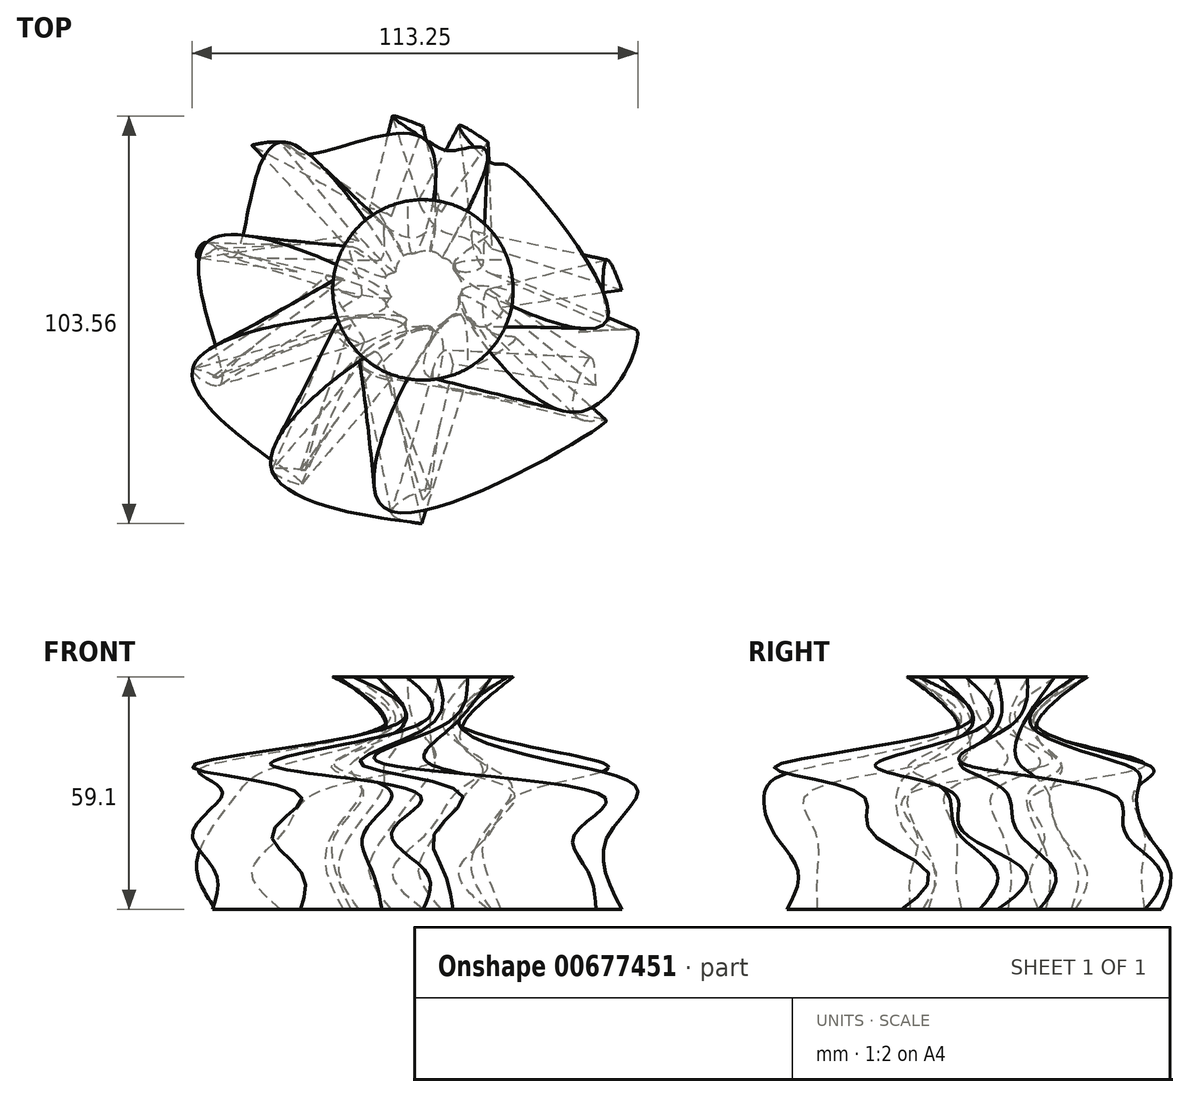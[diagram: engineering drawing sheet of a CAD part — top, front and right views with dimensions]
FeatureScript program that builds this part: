
annotation { "Feature Type Name" : "Feature", "Feature Type Description" : "" }
export const myFeature = defineFeature(function(context is Context, id is Id, definition is map)
    precondition{}
    {
        {
            var Q0;
            Q0=qCreatedBy(makeId("Top.planeOp"),FACE);
            var sketch = newSketch(context, id + "F0", { "sketchPlane" : qUnion([Q0])});
            skLineSegment(sketch, "E0", {"start": v(-7.97, 18.78) * mm, "end": v(0, 41.6) * mm});
            skLineSegment(sketch, "E1", {"start": v(0, 41.6) * mm, "end": v(4.74, 19.84) * mm});
            skLineSegment(sketch, "E2", {"start": v(4.74, 19.84) * mm, "end": v(16.58, 37.53) * mm});
            skLineSegment(sketch, "E3", {"start": v(16.58, 37.53) * mm, "end": v(17.47, 10.52) * mm});
            skLineSegment(sketch, "E4", {"start": v(19.88, -4.56) * mm, "end": v(43.93, -24.34) * mm});
            skLineSegment(sketch, "E5", {"start": v(43.93, -24.34) * mm, "end": v(7.69, -18.9) * mm});
            skLineSegment(sketch, "E6", {"start": v(7.69, -18.9) * mm, "end": v(0, -53.44) * mm});
            skLineSegment(sketch, "E7", {"start": v(0, -53.44) * mm, "end": v(-10.44, -17.52) * mm});
            skLineSegment(sketch, "E8", {"start": v(-10.44, -17.52) * mm, "end": v(-31.13, -45.68) * mm});
            skLineSegment(sketch, "E9", {"start": v(-31.13, -45.68) * mm, "end": v(-18.32, -8.97) * mm});
            skLineSegment(sketch, "E10", {"start": v(-18.32, -8.97) * mm, "end": v(-53.44, -22.02) * mm});
            skLineSegment(sketch, "E11", {"start": v(-53.44, -22.02) * mm, "end": v(-20.2, 2.78) * mm});
            skLineSegment(sketch, "E12", {"start": v(-20.2, 2.78) * mm, "end": v(-52.66, 10.52) * mm});
            skLineSegment(sketch, "E13", {"start": v(-52.66, 10.52) * mm, "end": v(-16.24, 12.35) * mm});
            skLineSegment(sketch, "E14", {"start": v(-16.24, 12.35) * mm, "end": v(-36.17, 37.53) * mm});
            skLineSegment(sketch, "E15", {"start": v(-36.17, 37.53) * mm, "end": v(-7.97, 18.78) * mm});
            skLineSegment(sketch, "E16", {"start": v(17.47, 10.52) * mm, "end": v(50.53, 0) * mm});
            skLineSegment(sketch, "E17", {"start": v(50.53, 0) * mm, "end": v(19.88, -4.56) * mm});
            skSolve(sketch);
        }
        {
            var Q0;
            Q0=qCreatedBy(makeId("Top.planeOp"),FACE);
            cPlane(context, id + "F1", {"entities" : qUnion([Q0]), "cplaneType" : CPlaneType.OFFSET, "offset" : 18.6 * mm, "width" : 150 * mm, "height" : 150 * mm});
        }
        {
            var Q0;
            Q0=qCreatedBy(makeId("Top.planeOp"),FACE);
            cPlane(context, id + "F2", {"entities" : qUnion([Q0]), "cplaneType" : CPlaneType.OFFSET, "offset" : 28.9 * mm, "width" : 150 * mm, "height" : 150 * mm});
        }
        {
            var Q0;
            Q0=qCreatedBy(id+"F1.planeOp",FACE);
            var sketch = newSketch(context, id + "F3", { "sketchPlane" : qUnion([Q0])});
            skLineSegment(sketch, "E18", {"start": v(-9.7, 16.39) * mm, "end": v(0.22, 38.44) * mm});
            skLineSegment(sketch, "E19", {"start": v(0.22, 38.44) * mm, "end": v(3.05, 16.34) * mm});
            skLineSegment(sketch, "E20", {"start": v(3.05, 16.34) * mm, "end": v(16.38, 32.93) * mm});
            skLineSegment(sketch, "E21", {"start": v(16.38, 32.93) * mm, "end": v(14.92, 5.95) * mm});
            skLineSegment(sketch, "E22", {"start": v(16, -9.28) * mm, "end": v(38.24, -31.09) * mm});
            skLineSegment(sketch, "E23", {"start": v(38.24, -31.09) * mm, "end": v(2.6, -22.5) * mm});
            skLineSegment(sketch, "E24", {"start": v(2.6, -22.5) * mm, "end": v(-8.07, -56.24) * mm});
            skLineSegment(sketch, "E25", {"start": v(-8.07, -56.24) * mm, "end": v(-15.34, -19.55) * mm});
            skLineSegment(sketch, "E26", {"start": v(-15.34, -19.55) * mm, "end": v(-38.4, -45.8) * mm});
            skLineSegment(sketch, "E27", {"start": v(-38.4, -45.8) * mm, "end": v(-22.44, -10.35) * mm});
            skLineSegment(sketch, "E28", {"start": v(-22.44, -10.35) * mm, "end": v(-58.56, -20.28) * mm});
            skLineSegment(sketch, "E29", {"start": v(-58.56, -20.28) * mm, "end": v(-23.3, 1.52) * mm});
            skLineSegment(sketch, "E30", {"start": v(-23.3, 1.52) * mm, "end": v(-54.95, 12.06) * mm});
            skLineSegment(sketch, "E31", {"start": v(-54.95, 12.06) * mm, "end": v(-18.5, 10.7) * mm});
            skLineSegment(sketch, "E32", {"start": v(-18.5, 10.7) * mm, "end": v(-36.17, 37.53) * mm});
            skLineSegment(sketch, "E33", {"start": v(-36.17, 37.53) * mm, "end": v(-9.7, 16.39) * mm});
            skLineSegment(sketch, "E34", {"start": v(14.92, 5.95) * mm, "end": v(46.93, -7.41) * mm});
            skLineSegment(sketch, "E35", {"start": v(46.93, -7.41) * mm, "end": v(16, -9.28) * mm});
            skSolve(sketch);
        }
        {
            var Q0;
            Q0=qCreatedBy(id+"F2.planeOp",FACE);
            var sketch = newSketch(context, id + "F4", { "sketchPlane" : qUnion([Q0])});
            skLineSegment(sketch, "E36", {"start": v(-2.22, 13.34) * mm, "end": v(7.7, 35.4) * mm});
            skLineSegment(sketch, "E37", {"start": v(7.7, 35.4) * mm, "end": v(10.53, 13.3) * mm});
            skLineSegment(sketch, "E38", {"start": v(10.53, 13.3) * mm, "end": v(23.87, 29.89) * mm});
            skLineSegment(sketch, "E39", {"start": v(23.87, 29.89) * mm, "end": v(22.4, 2.9) * mm});
            skLineSegment(sketch, "E40", {"start": v(23.49, -12.33) * mm, "end": v(45.72, -34.13) * mm});
            skLineSegment(sketch, "E41", {"start": v(45.72, -34.13) * mm, "end": v(10.1, -25.55) * mm});
            skLineSegment(sketch, "E42", {"start": v(10.1, -25.55) * mm, "end": v(-0.58, -59.29) * mm});
            skLineSegment(sketch, "E43", {"start": v(-0.58, -59.29) * mm, "end": v(-7.85, -22.6) * mm});
            skLineSegment(sketch, "E44", {"start": v(-7.85, -22.6) * mm, "end": v(-30.91, -48.85) * mm});
            skLineSegment(sketch, "E45", {"start": v(-30.91, -48.85) * mm, "end": v(-14.95, -13.4) * mm});
            skLineSegment(sketch, "E46", {"start": v(-14.95, -13.4) * mm, "end": v(-51.07, -23.33) * mm});
            skLineSegment(sketch, "E47", {"start": v(-51.07, -23.33) * mm, "end": v(-15.8, -1.53) * mm});
            skLineSegment(sketch, "E48", {"start": v(-15.8, -1.53) * mm, "end": v(-47.46, 9.01) * mm});
            skLineSegment(sketch, "E49", {"start": v(-47.46, 9.01) * mm, "end": v(-11.02, 7.66) * mm});
            skLineSegment(sketch, "E50", {"start": v(-11.02, 7.66) * mm, "end": v(-28.69, 34.49) * mm});
            skLineSegment(sketch, "E51", {"start": v(-28.69, 34.49) * mm, "end": v(-2.22, 13.34) * mm});
            skLineSegment(sketch, "E52", {"start": v(22.4, 2.9) * mm, "end": v(54.42, -10.46) * mm});
            skLineSegment(sketch, "E53", {"start": v(54.42, -10.46) * mm, "end": v(23.49, -12.33) * mm});
            skSolve(sketch);
        }
        {
            var Q0;
            Q0=qCreatedBy(makeId("Top.planeOp"),FACE);
            cPlane(context, id + "F5", {"entities" : qUnion([Q0]), "cplaneType" : CPlaneType.OFFSET, "offset" : 9.9 * mm, "width" : 150 * mm, "height" : 150 * mm});
        }
        {
            var Q0;
            Q0=qCreatedBy(id+"F5.planeOp",FACE);
            var sketch = newSketch(context, id + "F6", { "sketchPlane" : qUnion([Q0])});
            skLineSegment(sketch, "E54", {"start": v(-13.67, 20.55) * mm, "end": v(-7.73, 43.99) * mm});
            skLineSegment(sketch, "E55", {"start": v(-7.73, 43.99) * mm, "end": v(-1.1, 22.72) * mm});
            skLineSegment(sketch, "E56", {"start": v(-1.1, 22.72) * mm, "end": v(9.15, 41.37) * mm});
            skLineSegment(sketch, "E57", {"start": v(9.15, 41.37) * mm, "end": v(12.4, 14.54) * mm});
            skLineSegment(sketch, "E58", {"start": v(16.1, -0.27) * mm, "end": v(41.79, -17.88) * mm});
            skLineSegment(sketch, "E59", {"start": v(41.79, -17.88) * mm, "end": v(5.2, -15.61) * mm});
            skLineSegment(sketch, "E60", {"start": v(5.2, -15.61) * mm, "end": v(0.56, -50.7) * mm});
            skLineSegment(sketch, "E61", {"start": v(0.56, -50.7) * mm, "end": v(-12.98, -15.82) * mm});
            skLineSegment(sketch, "E62", {"start": v(-12.98, -15.82) * mm, "end": v(-31.13, -45.68) * mm});
            skLineSegment(sketch, "E63", {"start": v(-31.13, -45.68) * mm, "end": v(-21.57, -8) * mm});
            skLineSegment(sketch, "E64", {"start": v(-18.32, -8.97) * mm, "end": v(-53.44, -22.02) * mm});
            skLineSegment(sketch, "E65", {"start": v(-55.42, -24.05) * mm, "end": v(-24.47, 3.55) * mm});
            skLineSegment(sketch, "E66", {"start": v(-24.47, 3.55) * mm, "end": v(-57.48, 8.43) * mm});
            skLineSegment(sketch, "E67", {"start": v(-57.48, 8.43) * mm, "end": v(-21.35, 13.42) * mm});
            skLineSegment(sketch, "E68", {"start": v(-21.35, 13.42) * mm, "end": v(-43.4, 36.78) * mm});
            skLineSegment(sketch, "E69", {"start": v(-43.4, 36.78) * mm, "end": v(-13.67, 20.55) * mm});
            skLineSegment(sketch, "E70", {"start": v(12.4, 14.54) * mm, "end": v(46.24, 6.94) * mm});
            skLineSegment(sketch, "E71", {"start": v(46.24, 6.94) * mm, "end": v(16.1, -0.27) * mm});
            skSolve(sketch);
        }
        {
            var Q0;
            Q0=qCreatedBy(makeId("Top.planeOp"),FACE);
            cPlane(context, id + "F7", {"entities" : qUnion([Q0]), "cplaneType" : CPlaneType.OFFSET, "offset" : 36.6 * mm, "width" : 150 * mm, "height" : 150 * mm});
        }
        {
            var Q0;
            Q0=qCreatedBy(id+"F7.planeOp",FACE);
            var sketch = newSketch(context, id + "F8", { "sketchPlane" : qUnion([Q0])});
            skLineSegment(sketch, "E72", {"start": v(-9.7, 16.39) * mm, "end": v(0.22, 38.44) * mm});
            skLineSegment(sketch, "E73", {"start": v(0.22, 38.44) * mm, "end": v(3.05, 16.34) * mm});
            skLineSegment(sketch, "E74", {"start": v(3.05, 16.34) * mm, "end": v(16.38, 32.93) * mm});
            skLineSegment(sketch, "E75", {"start": v(16.38, 32.93) * mm, "end": v(14.92, 5.95) * mm});
            skLineSegment(sketch, "E76", {"start": v(16, -9.28) * mm, "end": v(38.24, -31.09) * mm});
            skLineSegment(sketch, "E77", {"start": v(38.24, -31.09) * mm, "end": v(2.6, -22.5) * mm});
            skLineSegment(sketch, "E78", {"start": v(2.6, -22.5) * mm, "end": v(-8.07, -56.24) * mm});
            skLineSegment(sketch, "E79", {"start": v(-8.07, -56.24) * mm, "end": v(-15.34, -19.55) * mm});
            skLineSegment(sketch, "E80", {"start": v(-15.34, -19.55) * mm, "end": v(-38.4, -45.8) * mm});
            skLineSegment(sketch, "E81", {"start": v(-38.4, -45.8) * mm, "end": v(-22.44, -10.35) * mm});
            skLineSegment(sketch, "E82", {"start": v(-22.44, -10.35) * mm, "end": v(-58.56, -20.28) * mm});
            skLineSegment(sketch, "E83", {"start": v(-58.56, -20.28) * mm, "end": v(-23.3, 1.52) * mm});
            skLineSegment(sketch, "E84", {"start": v(-23.3, 1.52) * mm, "end": v(-54.95, 12.06) * mm});
            skLineSegment(sketch, "E85", {"start": v(-54.95, 12.06) * mm, "end": v(-18.5, 10.7) * mm});
            skLineSegment(sketch, "E86", {"start": v(-18.5, 10.7) * mm, "end": v(-36.17, 37.53) * mm});
            skLineSegment(sketch, "E87", {"start": v(-36.17, 37.53) * mm, "end": v(-9.7, 16.39) * mm});
            skLineSegment(sketch, "E88", {"start": v(14.92, 5.95) * mm, "end": v(46.93, -7.41) * mm});
            skLineSegment(sketch, "E89", {"start": v(46.93, -7.41) * mm, "end": v(16, -9.28) * mm});
            skSolve(sketch);
        }
        {
            var Q0;
            Q0=qCreatedBy(makeId("Top.planeOp"),FACE);
            cPlane(context, id + "F9", {"entities" : qUnion([Q0]), "cplaneType" : CPlaneType.OFFSET, "offset" : 46.7 * mm, "width" : 150 * mm, "height" : 150 * mm});
        }
        {
            var Q0;
            Q0=qCreatedBy(makeId("Top.planeOp"),FACE);
            cPlane(context, id + "F10", {"entities" : qUnion([Q0]), "cplaneType" : CPlaneType.OFFSET, "offset" : 59.1 * mm, "width" : 150 * mm, "height" : 150 * mm});
        }
        {
            var Q0;
            Q0=qCreatedBy(id+"F9.planeOp",FACE);
            var sketch = newSketch(context, id + "F11", { "sketchPlane" : qUnion([Q0])});
            skCircle(sketch, "E90", {"center": v(0, 0) * mm, "radius": 10.02 * mm});
            skSolve(sketch);
        }
        {
            var Q0;
            Q0=qCreatedBy(id+"F10.planeOp",FACE);
            var sketch = newSketch(context, id + "F12", { "sketchPlane" : qUnion([Q0])});
            skCircle(sketch, "E91", {"center": v(0, 0) * mm, "radius": 22.92 * mm});
            skSolve(sketch);
        }
        {
            var Q0;
            Q0=makeQuery(id+"F0.imprint","IMPRINT",FACE,{"disambiguationData":[TD([[makeQuery(id+"F0.imprint","IMPRINT",EDGE,{"derivedFrom":sQuery(id+"F0.wireOp",EDGE,"E0")}),-1.0]])]});
            var Q1;
            Q1=makeQuery(id+"F6.imprint","IMPRINT",FACE,{"disambiguationData":[TD([[makeQuery(id+"F6.imprint","IMPRINT",EDGE,{"derivedFrom":sQuery(id+"F6.wireOp",EDGE,"E54")}),-1.0]])]});
            var Q2;
            Q2=makeQuery(id+"F3.imprint","IMPRINT",FACE,{"disambiguationData":[TD([[makeQuery(id+"F3.imprint","IMPRINT",EDGE,{"derivedFrom":sQuery(id+"F3.wireOp",EDGE,"E18")}),-1.0]])]});
            var Q3;
            Q3=makeQuery(id+"F4.imprint","IMPRINT",FACE,{"disambiguationData":[TD([[makeQuery(id+"F4.imprint","IMPRINT",EDGE,{"derivedFrom":sQuery(id+"F4.wireOp",EDGE,"E36")}),-1.0]])]});
            var Q4;
            Q4=makeQuery(id+"F8.imprint","IMPRINT",FACE,{"disambiguationData":[TD([[makeQuery(id+"F8.imprint","IMPRINT",EDGE,{"derivedFrom":sQuery(id+"F8.wireOp",EDGE,"E72")}),-1.0]])]});
            var Q5;
            Q5=makeQuery(id+"F11.imprint","IMPRINT",FACE,{"disambiguationData":[TD([[makeQuery(id+"F11.imprint","IMPRINT",EDGE,{"derivedFrom":sQuery(id+"F11.wireOp",EDGE,"E90")}),1.0]])]});
            var Q6;
            Q6=makeQuery(id+"F12.imprint","IMPRINT",FACE,{"disambiguationData":[TD([[makeQuery(id+"F12.imprint","IMPRINT",EDGE,{"derivedFrom":sQuery(id+"F12.wireOp",EDGE,"E91")}),1.0]])]});
            loft(context, id + "F13", {"sheetProfilesArray" : [{ "sheetProfileEntities" : qUnion([Q0]) }, { "sheetProfileEntities" : qUnion([Q1]) }, { "sheetProfileEntities" : qUnion([Q2]) }, { "sheetProfileEntities" : qUnion([Q3]) }, { "sheetProfileEntities" : qUnion([Q4]) }, { "sheetProfileEntities" : qUnion([Q5]) }, { "sheetProfileEntities" : qUnion([Q6]) }]});
        }
    });
